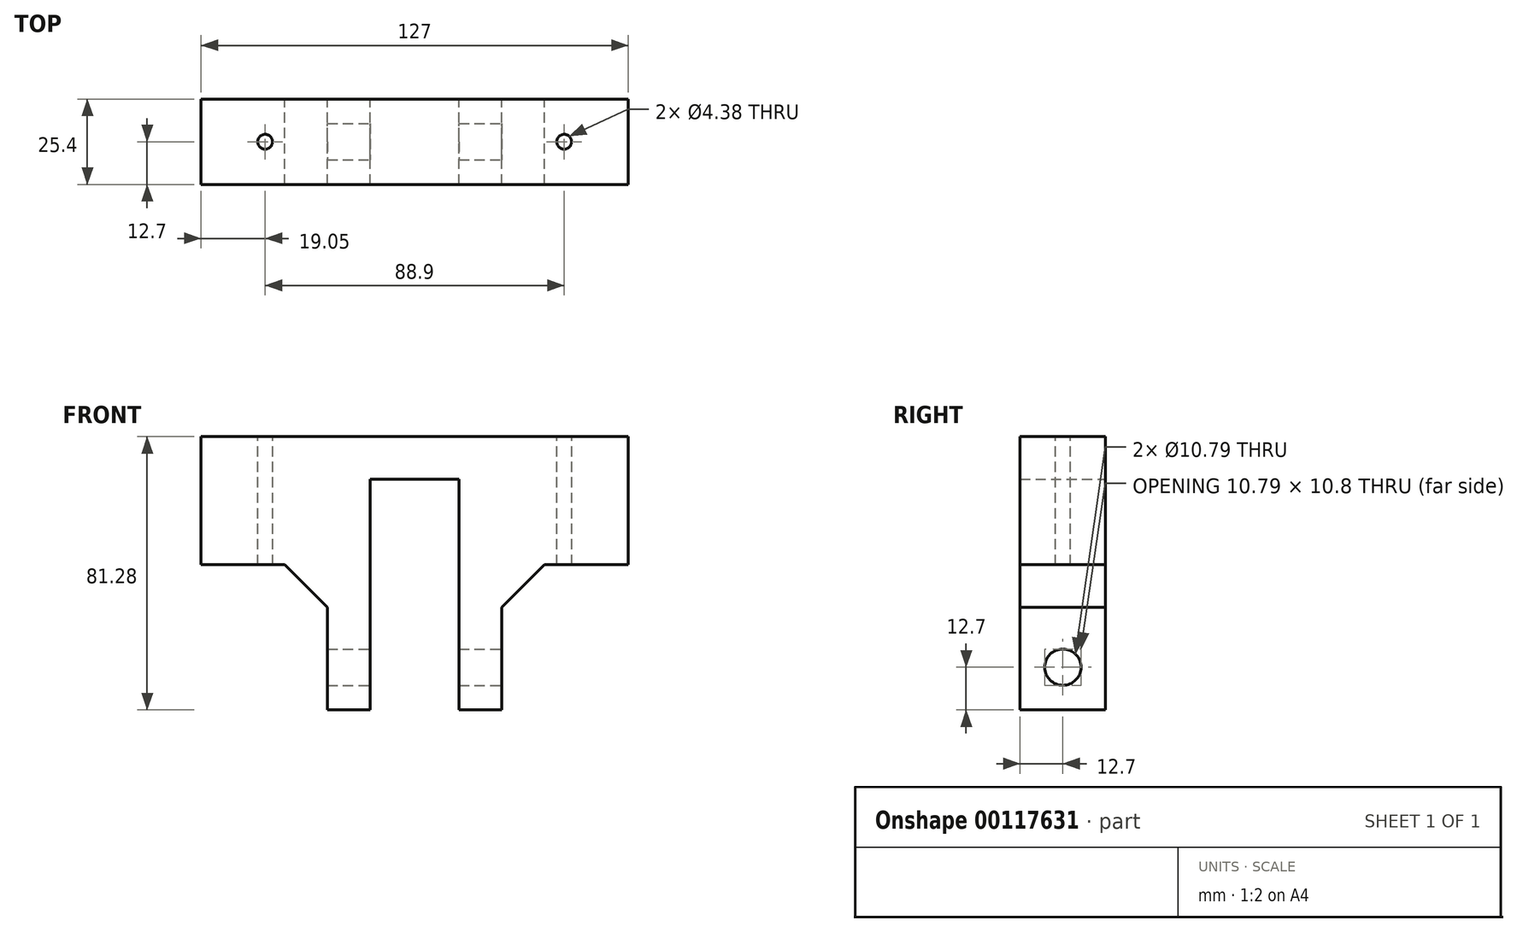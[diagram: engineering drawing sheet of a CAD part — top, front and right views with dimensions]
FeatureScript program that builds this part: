
annotation { "Feature Type Name" : "Feature", "Feature Type Description" : "" }
export const myFeature = defineFeature(function(context is Context, id is Id, definition is map)
    precondition{}
    {
        {
            var Q0;
            Q0=qCreatedBy(makeId("Front.planeOp"),FACE);
            var sketch = newSketch(context, id + "F0", { "sketchPlane" : qUnion([Q0])});
            skLineSegment(sketch, "E0", {"start": v(38.6, -38.1) * mm, "end": v(25.9, -50.8) * mm});
            skLineSegment(sketch, "E1", {"start": v(25.9, -50.8) * mm, "end": v(25.9, -81.28) * mm});
            skLineSegment(sketch, "E2", {"start": v(25.9, -81.28) * mm, "end": v(13.2, -81.28) * mm});
            skLineSegment(sketch, "E3", {"start": v(13.2, -81.28) * mm, "end": v(13.2, -12.7) * mm});
            skLineSegment(sketch, "E4", {"start": v(13.2, -12.7) * mm, "end": v(-13.2, -12.7) * mm});
            skLineSegment(sketch, "E5", {"start": v(-13.2, -12.7) * mm, "end": v(-13.2, -81.28) * mm});
            skLineSegment(sketch, "E6", {"start": v(-13.2, -81.28) * mm, "end": v(-25.9, -81.28) * mm});
            skLineSegment(sketch, "E7", {"start": v(-25.9, -81.28) * mm, "end": v(-25.9, -50.8) * mm});
            skLineSegment(sketch, "E8", {"start": v(-25.9, -50.8) * mm, "end": v(-38.6, -38.1) * mm});
            skLineSegment(sketch, "E9", {"start": v(0, 0) * mm, "end": v(-63.5, 0) * mm});
            skLineSegment(sketch, "E10", {"start": v(0, 0) * mm, "end": v(63.5, 0) * mm});
            skLineSegment(sketch, "E11", {"start": v(-63.5, 0) * mm, "end": v(-63.5, -38.1) * mm});
            skLineSegment(sketch, "E12", {"start": v(-63.5, -38.1) * mm, "end": v(-38.6, -38.1) * mm});
            skLineSegment(sketch, "E13", {"start": v(63.5, 0) * mm, "end": v(63.5, -38.1) * mm});
            skLineSegment(sketch, "E14", {"start": v(63.5, -38.1) * mm, "end": v(38.6, -38.1) * mm});
            skSolve(sketch);
        }
        {
            var Q0;
            Q0=makeQuery(id+"F0.imprint","IMPRINT",FACE,{"disambiguationData":[TD([[makeQuery(id+"F0.imprint","IMPRINT",EDGE,{"derivedFrom":sQuery(id+"F0.wireOp",EDGE,"E0")}),-1.0]])]});
            var Q1;
            Q1=sQuery(id+"F0.wireOp",EDGE,"E0");
            var Q2;
            Q2=sQuery(id+"F0.wireOp",EDGE,"E1");
            var Q3;
            Q3=sQuery(id+"F0.wireOp",EDGE,"E2");
            var Q4;
            Q4=sQuery(id+"F0.wireOp",EDGE,"E3");
            var Q5;
            Q5=sQuery(id+"F0.wireOp",EDGE,"E4");
            var Q6;
            Q6=sQuery(id+"F0.wireOp",EDGE,"E5");
            var Q7;
            Q7=sQuery(id+"F0.wireOp",EDGE,"E6");
            var Q8;
            Q8=sQuery(id+"F0.wireOp",EDGE,"E7");
            var Q9;
            Q9=sQuery(id+"F0.wireOp",EDGE,"E8");
            var Q10;
            Q10=sQuery(id+"F0.wireOp",EDGE,"E9");
            var Q11;
            Q11=sQuery(id+"F0.wireOp",EDGE,"E10");
            var Q12;
            Q12=sQuery(id+"F0.wireOp",EDGE,"E11");
            var Q13;
            Q13=sQuery(id+"F0.wireOp",EDGE,"E12");
            var Q14;
            Q14=sQuery(id+"F0.wireOp",EDGE,"E13");
            var Q15;
            Q15=sQuery(id+"F0.wireOp",EDGE,"E14");
            extrude(context, id + "F1", {"entities" : qUnion([Q0]), "surfaceEntities" : qUnion([Q1, Q2, Q3, Q4, Q5, Q6, Q7, Q8, Q9, Q10, Q11, Q12, Q13, Q14, Q15]), "depth" : 25.4 * mm});
        }
        {
            var Q0;
            Q0=makeQuery(id+"F1.opExtrude","SWEPT_FACE",FACE,{"disambiguationData":[OSD([sQuery(id+"F0.wireOp",EDGE,"E9"),sQuery(id+"F0.wireOp",EDGE,"E10")])]});
            var sketch = newSketch(context, id + "F2", { "sketchPlane" : qUnion([Q0])});
            skCircle(sketch, "E15", {"center": v(-44.45, -12.7) * mm, "radius": 2.2 * mm});
            skPoint(sketch, "E15.centerSnap0", {"position": v(-63.5, -12.7) * mm});
            skCircle(sketch, "E16.MirrorC", {"center": v(44.45, -12.7) * mm, "radius": 2.2 * mm});
            skSolve(sketch);
        }
        {
            var Q0;
            Q0 = qSketchRegion(id + "F2", true);
            extrude(context, id + "F3", {"entities" : qUnion([Q0]), "operationType" : NewBodyOperationType.REMOVE, "endBound" : BoundingType.THROUGH_ALL, "oppositeDirection" : true, "depth" : 25.4 * mm});
        }
        {
            var Q0;
            Q0=makeQuery(id+"F1.opExtrude","SWEPT_FACE",FACE,{"disambiguationData":[OSD([sQuery(id+"F0.wireOp",EDGE,"E1")])]});
            var sketch = newSketch(context, id + "F4", { "sketchPlane" : qUnion([Q0])});
            skCircle(sketch, "E17", {"center": v(-12.7, -68.58) * mm, "radius": 5.4 * mm});
            skPoint(sketch, "E17.centerSnap0", {"position": v(-12.7, -81.28) * mm});
            skSolve(sketch);
        }
        {
            var Q0;
            Q0=makeQuery(id+"F4.imprint","IMPRINT",FACE,{"disambiguationData":[TD([[makeQuery(id+"F4.imprint","IMPRINT",EDGE,{"derivedFrom":sQuery(id+"F4.wireOp",EDGE,"E17")}),1.0]])]});
            extrude(context, id + "F5", {"entities" : qUnion([Q0]), "operationType" : NewBodyOperationType.REMOVE, "endBound" : BoundingType.THROUGH_ALL, "oppositeDirection" : true, "depth" : 25.4 * mm});
        }
    });
